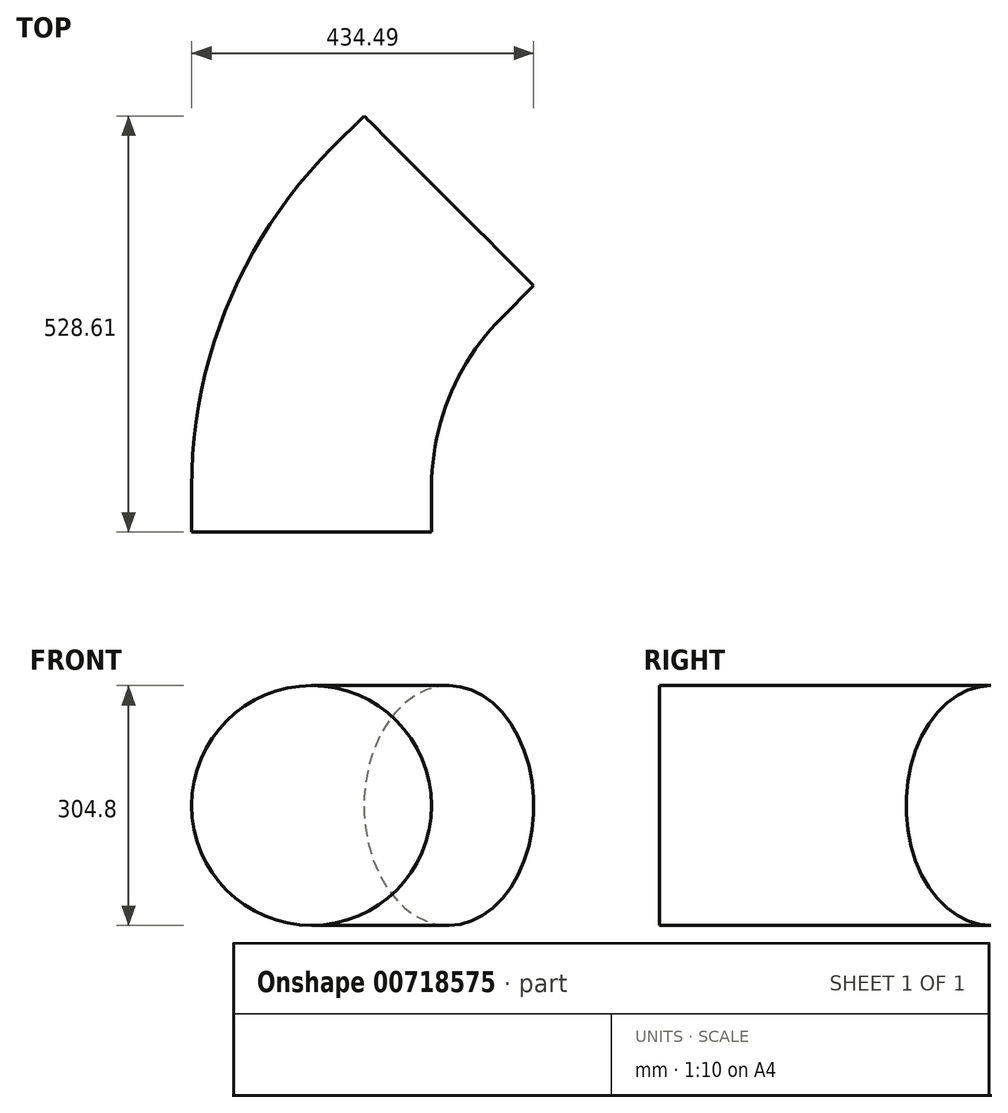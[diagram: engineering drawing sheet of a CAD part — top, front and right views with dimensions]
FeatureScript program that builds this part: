
annotation { "Feature Type Name" : "Feature", "Feature Type Description" : "" }
export const myFeature = defineFeature(function(context is Context, id is Id, definition is map)
    precondition{}
    {
        {
            var Q0;
            Q0=qCreatedBy(makeId("Front.planeOp"),FACE);
            var sketch = newSketch(context, id + "F0", { "sketchPlane" : qUnion([Q0])});
            skLineSegment(sketch, "E0", {"start": v(0, 0) * mm, "end": v(-457.2, 0) * mm, "construction": true});
            skCircle(sketch, "E1", {"center": v(-457.2, 0) * mm, "radius": 152.4 * mm});
            skSolve(sketch);
        }
        {
            var Q0;
            Q0=qCreatedBy(makeId("Top.planeOp"),FACE);
            var sketch = newSketch(context, id + "F1", { "sketchPlane" : qUnion([Q0])});
            skArc(sketch, "E2", {"start": v(-323.29, 323.29) * mm, "mid": v(-422.4, 174.96) * mm, "end": v(-457.2, 0) * mm});
            skLineSegment(sketch, "E3", {"start": v(0, 0) * mm, "end": v(-505.33, 0) * mm, "construction": true});
            skLineSegment(sketch, "E4", {"start": v(0, 0) * mm, "end": v(0, 518.45) * mm, "construction": true});
            skLineSegment(sketch, "E5", {"start": v(0, 0) * mm, "end": v(-418.7, 418.7) * mm, "construction": true});
            skSolve(sketch);
        }
        {
            var Q0;
            Q0=makeQuery(id+"F0.imprint","IMPRINT",FACE,{"disambiguationData":[TD([[makeQuery(id+"F0.imprint","IMPRINT",EDGE,{"derivedFrom":sQuery(id+"F0.wireOp",EDGE,"E1")}),1.0]])]});
            var Q1;
            Q1=qConstructionFilter(qBodyType(qCreatedBy(id+"F1",EDGE),BodyType.WIRE),ConstructionObject.NO);
            sweep(context, id + "F2", {"profiles" : qUnion([Q0]), "path" : qUnion([Q1])});
        }
        {
            var Q0;
            Q0=makeQuery(id+"F2.opSweep","CAP_FACE",FACE,{"disambiguationData":[OSD([sQuery(id+"F0.wireOp",EDGE,"E1"),sQuery(id+"F1.wireOp",VERTEX,"E2.end")])],"isStart":true});
            extrude(context, id + "F3", {"entities" : qUnion([Q0]), "operationType" : NewBodyOperationType.ADD, "depth" : 57.15 * mm, "offsetDistance" : 25.4 * mm});
        }
        {
            var Q0;
            Q0=makeQuery(id+"F2.opSweep","CAP_FACE",FACE,{"disambiguationData":[OSD([sQuery(id+"F0.wireOp",EDGE,"E1"),sQuery(id+"F1.wireOp",VERTEX,"E2.start")])],"isStart":false});
            extrude(context, id + "F4", {"entities" : qUnion([Q0]), "operationType" : NewBodyOperationType.ADD, "depth" : 57.15 * mm, "offsetDistance" : 25.4 * mm});
        }
    });
